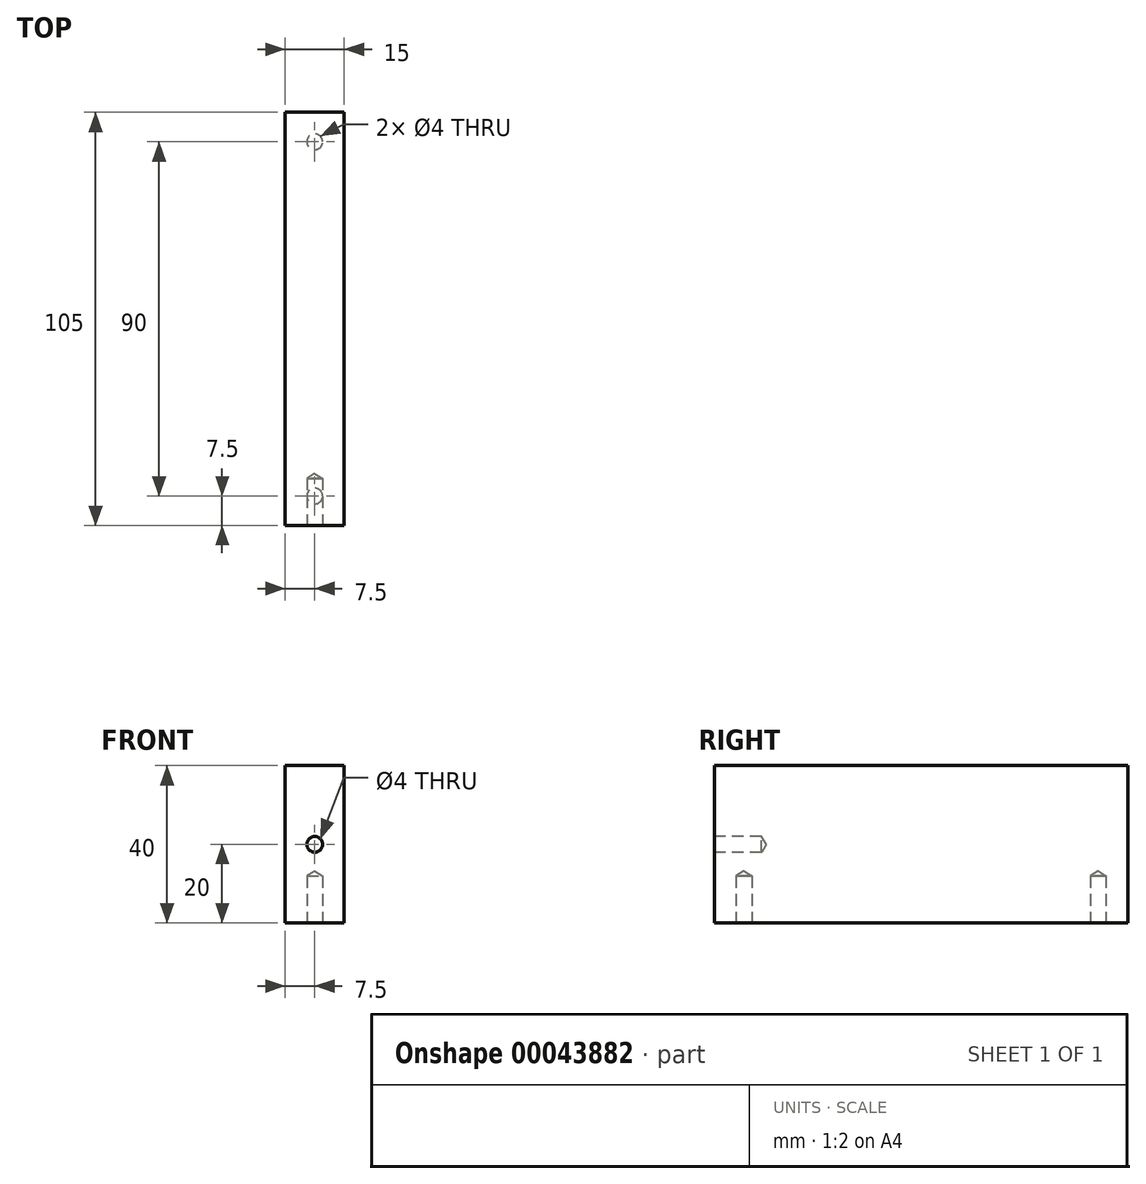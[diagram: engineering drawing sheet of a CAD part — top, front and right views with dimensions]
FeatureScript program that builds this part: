
annotation { "Feature Type Name" : "Feature", "Feature Type Description" : "" }
export const myFeature = defineFeature(function(context is Context, id is Id, definition is map)
    precondition{}
    {
        {
            var Q0;
            Q0=qCreatedBy(makeId("Right.planeOp"),FACE);
            var sketch = newSketch(context, id + "F0", { "sketchPlane" : qUnion([Q0])});
            skLineSegment(sketch, "E0.rect.bottom", {"start": v(52.5, 20) * mm, "end": v(-52.5, 20) * mm});
            skLineSegment(sketch, "E0.rect.top", {"start": v(52.5, -20) * mm, "end": v(-52.5, -20) * mm});
            skLineSegment(sketch, "E0.rect.left", {"start": v(52.5, 20) * mm, "end": v(52.5, -20) * mm});
            skLineSegment(sketch, "E0.rect.right", {"start": v(-52.5, 20) * mm, "end": v(-52.5, -20) * mm});
            skPoint(sketch, "E0.rect.middle", {"position": v(0, 0) * mm});
            skSolve(sketch);
        }
        {
            var Q0;
            Q0=makeQuery(id+"F0.imprint","IMPRINT",FACE,{"disambiguationData":[TD([[makeQuery(id+"F0.imprint","IMPRINT",EDGE,{"derivedFrom":sQuery(id+"F0.wireOp",EDGE,"E0.rect.bottom")}),1.0]])]});
            extrude(context, id + "F1", {"entities" : qUnion([Q0]), "depth" : 15 * mm});
        }
        {
            var Q0;
            Q0=makeQuery(id+"F1.opExtrude","SWEPT_FACE",FACE,{"disambiguationData":[OSD([sQuery(id+"F0.wireOp",EDGE,"E0.rect.right")])]});
            var sketch = newSketch(context, id + "F2", { "sketchPlane" : qUnion([Q0])});
            skPoint(sketch, "E1", {"position": v(7.5, 0) * mm});
            skLineSegment(sketch, "E2", {"start": v(0, 0) * mm, "end": v(15, 0) * mm});
            skSolve(sketch);
        }
        {
            var Q0;
            Q0=sQuery(id+"F2.wireOp",VERTEX,"E1");
            var Q1;
            Q1=makeQuery(id+"F1.opExtrude","SWEPT_BODY",BODY,{"disambiguationData":[OSD([sQuery(id+"F0.wireOp",EDGE,"E0.rect.bottom"),sQuery(id+"F0.wireOp",EDGE,"E0.rect.top"),sQuery(id+"F0.wireOp",EDGE,"E0.rect.left"),sQuery(id+"F0.wireOp",EDGE,"E0.rect.right")])]});
            hole(context, id + "F3", {"style" : HoleStyle.SIMPLE, "holeDiameter" : 4 * mm, "endStyle" : HoleEndStyle.BLIND, "holeDepth" : 12 * mm, "locations" : qUnion([Q0]), "scope" : qUnion([Q1])});
        }
        {
            var Q0;
            Q0=makeQuery(id+"F1.opExtrude","SWEPT_FACE",FACE,{"disambiguationData":[OSD([sQuery(id+"F0.wireOp",EDGE,"E0.rect.top")])]});
            var sketch = newSketch(context, id + "F4", { "sketchPlane" : qUnion([Q0])});
            skLineSegment(sketch, "E3", {"start": v(7.5, -45) * mm, "end": v(7.5, 45) * mm});
            skSolve(sketch);
        }
        {
            var Q0;
            Q0=sQuery(id+"F4.wireOp",VERTEX,"E3.end");
            var Q1;
            Q1=sQuery(id+"F4.wireOp",VERTEX,"E3.start");
            var Q2;
            Q2=makeQuery(id+"F1.opExtrude","SWEPT_BODY",BODY,{"disambiguationData":[OSD([sQuery(id+"F0.wireOp",EDGE,"E0.rect.bottom"),sQuery(id+"F0.wireOp",EDGE,"E0.rect.top"),sQuery(id+"F0.wireOp",EDGE,"E0.rect.left"),sQuery(id+"F0.wireOp",EDGE,"E0.rect.right")])]});
            hole(context, id + "F5", {"style" : HoleStyle.SIMPLE, "holeDiameter" : 4 * mm, "endStyle" : HoleEndStyle.BLIND, "holeDepth" : 12 * mm, "locations" : qUnion([Q0, Q1]), "scope" : qUnion([Q2])});
        }
    });
